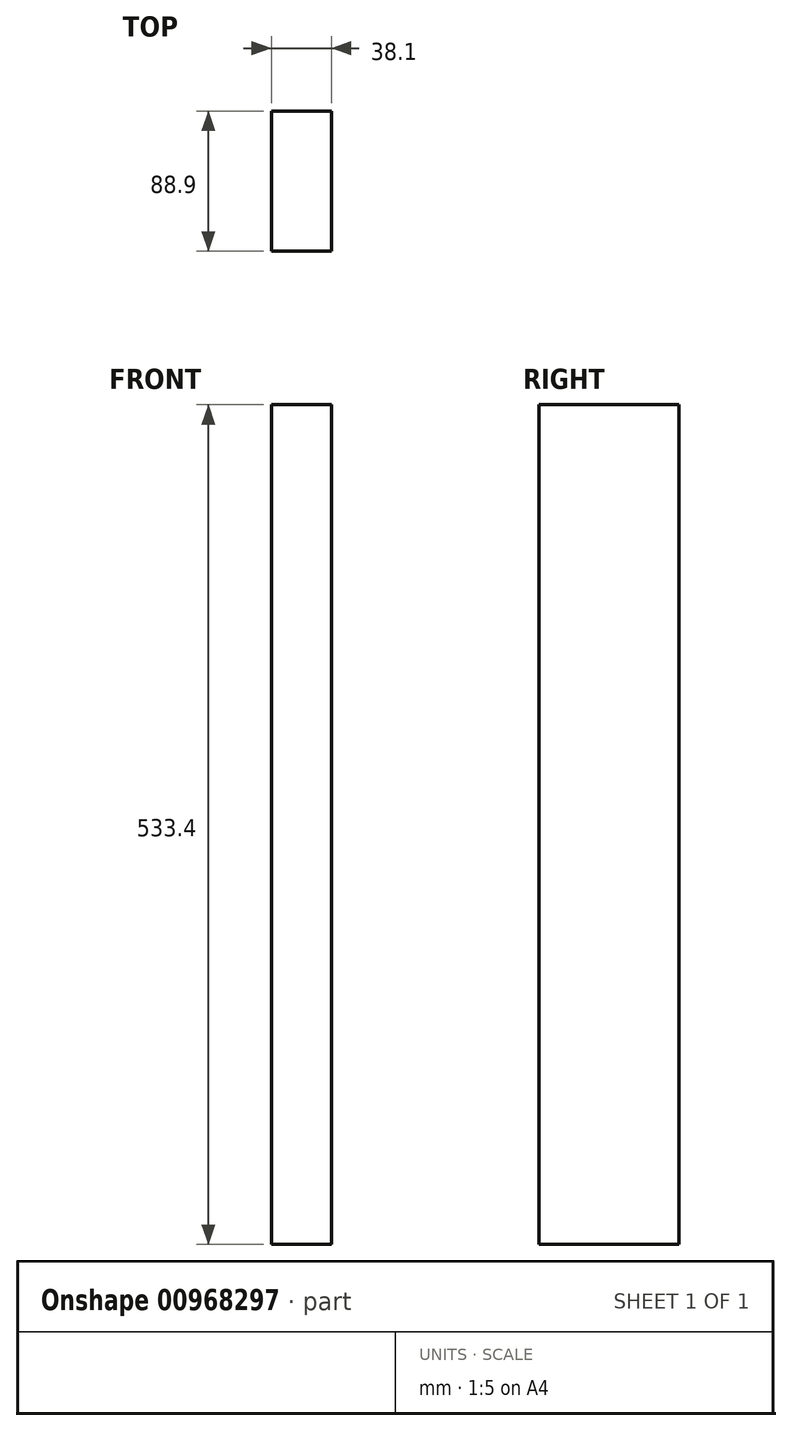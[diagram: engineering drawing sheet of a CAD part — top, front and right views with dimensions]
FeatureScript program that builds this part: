
annotation { "Feature Type Name" : "Feature", "Feature Type Description" : "" }
export const myFeature = defineFeature(function(context is Context, id is Id, definition is map)
    precondition{}
    {
        {
            var Q0;
            Q0=qCreatedBy(makeId("Top.planeOp"),FACE);
            var sketch = newSketch(context, id + "F0", { "sketchPlane" : qUnion([Q0])});
            skLineSegment(sketch, "E0.bottom", {"start": v(19.05, 44.45) * mm, "end": v(-19.05, 44.45) * mm});
            skLineSegment(sketch, "E0.top", {"start": v(19.05, -44.45) * mm, "end": v(-19.05, -44.45) * mm});
            skLineSegment(sketch, "E0.left", {"start": v(19.05, 44.45) * mm, "end": v(19.05, -44.45) * mm});
            skLineSegment(sketch, "E0.right", {"start": v(-19.05, 44.45) * mm, "end": v(-19.05, -44.45) * mm});
            skPoint(sketch, "E0.middle", {"position": v(0, 0) * mm});
            skSolve(sketch);
        }
        {
            var Q0;
            Q0=makeQuery(id+"F0.imprint","IMPRINT",FACE,{"disambiguationData":[TD([[makeQuery(id+"F0.imprint","IMPRINT",EDGE,{"derivedFrom":sQuery(id+"F0.wireOp",EDGE,"E0.bottom")}),1.0]])]});
            extrude(context, id + "F1", {"entities" : qUnion([Q0]), "endBound" : BoundingType.SYMMETRIC, "depth" : 533.4 * mm, "offsetDistance" : 25.4 * mm});
        }
    });
